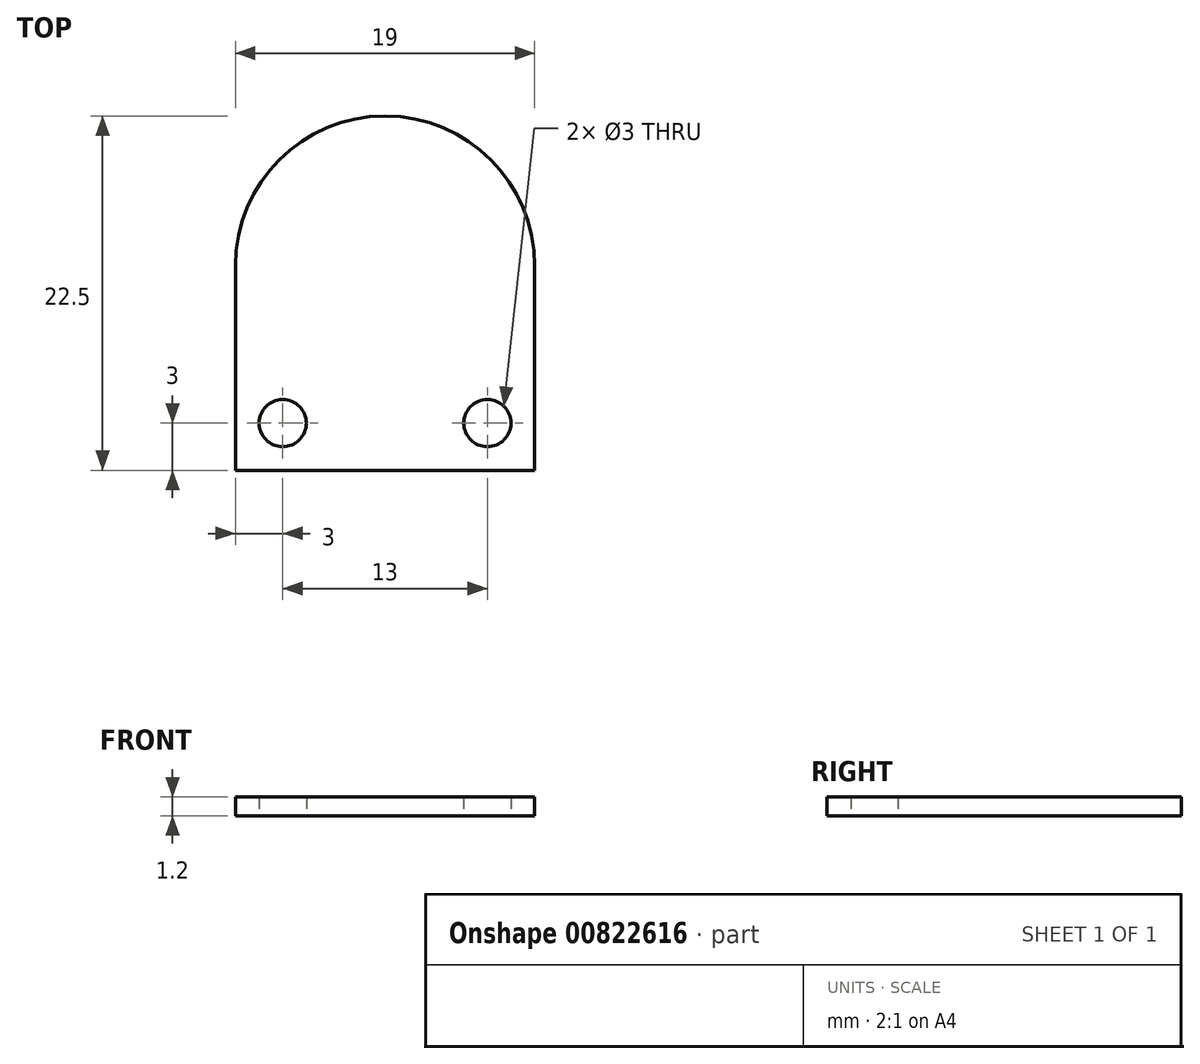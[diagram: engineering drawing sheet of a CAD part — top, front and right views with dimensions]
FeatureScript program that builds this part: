
annotation { "Feature Type Name" : "Feature", "Feature Type Description" : "" }
export const myFeature = defineFeature(function(context is Context, id is Id, definition is map)
    precondition{}
    {
        {
            var Q0;
            Q0=qCreatedBy(makeId("Top.planeOp"),FACE);
            var sketch = newSketch(context, id + "F0", { "sketchPlane" : qUnion([Q0])});
            skCircle(sketch, "E0", {"center": v(0, 0) * mm, "radius": 9.5 * mm});
            skLineSegment(sketch, "E1.bottom", {"start": v(-9.5, 0) * mm, "end": v(9.5, 0) * mm});
            skLineSegment(sketch, "E1.top", {"start": v(-9.5, -13) * mm, "end": v(9.5, -13) * mm});
            skLineSegment(sketch, "E1.left", {"start": v(-9.5, 0) * mm, "end": v(-9.5, -13) * mm});
            skLineSegment(sketch, "E1.right", {"start": v(9.5, 0) * mm, "end": v(9.5, -13) * mm});
            skPoint(sketch, "E2", {"position": v(0, 7.5) * mm});
            skCircle(sketch, "E3", {"center": v(-6.5, -10) * mm, "radius": 1.5 * mm});
            skCircle(sketch, "E4", {"center": v(6.5, -10) * mm, "radius": 1.5 * mm});
            skSolve(sketch);
        }
        {
            var Q0;
            {var subQ0=sQuery(id+"F0.wireOp",EDGE,"E1.bottom");Q0=makeQuery(id+"F0.imprint","IMPRINT",FACE,{"disambiguationData":[TD([[makeQuery(id+"F0.imprint","IMPRINT",EDGE,{"derivedFrom":subQ0}),1.0]])]});}
            var Q1;
            {var subQ0=sQuery(id+"F0.wireOp",EDGE,"E1.bottom");Q1=makeQuery(id+"F0.imprint","IMPRINT",FACE,{"disambiguationData":[TD([[makeQuery(id+"F0.imprint","IMPRINT",EDGE,{"derivedFrom":subQ0}),-1.0]])]});}
            var Q2;
            Q2=makeQuery(id+"F0.imprint","IMPRINT",FACE,{"disambiguationData":[TD([[makeQuery(id+"F0.imprint","IMPRINT",EDGE,{"derivedFrom":sQuery(id+"F0.wireOp",EDGE,"E1.top")}),1.0]])]});
            extrude(context, id + "F1", {"entities" : qUnion([Q0, Q1, Q2]), "depth" : 1.2 * mm, "offsetDistance" : 25 * mm});
        }
    });
